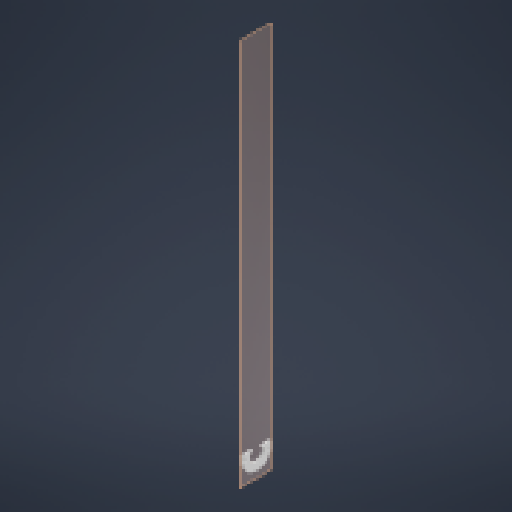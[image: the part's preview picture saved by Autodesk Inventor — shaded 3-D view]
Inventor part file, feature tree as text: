
AUTODESK INVENTOR PART (.ipt)
format: ipt  version: 2024.1 (Build 281209000, 209)  size: 146,944 bytes
history: native  units: in
note: dims shown in document units (in); Inventor stores cm internally (conversion verified against a paired STEP export)
features: other x3, plane x1, extrude x1, fillet x1, sketch x1, reference x1
ambient origin geometry x8: Origin, YZ Plane, XZ Plane, XY Plane, X Axis, Y Axis, Z Axis, Center Point
bodies: Solid1 (feature_tree)
feature tree (8):
  plane  "Work Plane1"
  extrude  "Extrusion1"  Depth=0.1181in TaperAngle=0.0deg
  fillet  "Fillet1"  Radius=0.25in
  sketch  "Sketch1"  dims[d0=0.7in d1=0.1181in d2=0.0in d3=0.25in]
  reference  "Reference1"
  other  "<userpath>\Documents\School\FallCAD\Trebuchet\Trebuchet.iam"
  other  "Trebuchet.iam"
  other  "DropBar:1"
